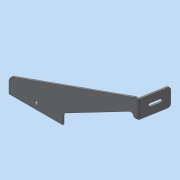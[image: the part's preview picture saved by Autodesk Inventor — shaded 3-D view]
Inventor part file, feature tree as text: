
AUTODESK INVENTOR PART (.ipt)
format: ipt  version: 2020 (Build 240168000, 168)  size: 173,568 bytes
history: native  units: mm
features: other x2, extrude x1
ambient origin geometry x8: Origin, YZ Plane, XZ Plane, XY Plane, X Axis, Y Axis, Z Axis, Center Point
bodies: Body1 (feature_tree)
feature tree (3):
  other  "實體1"
  extrude  "擠出1"  Depth=130.0mm
  other  "折彎零件1"
